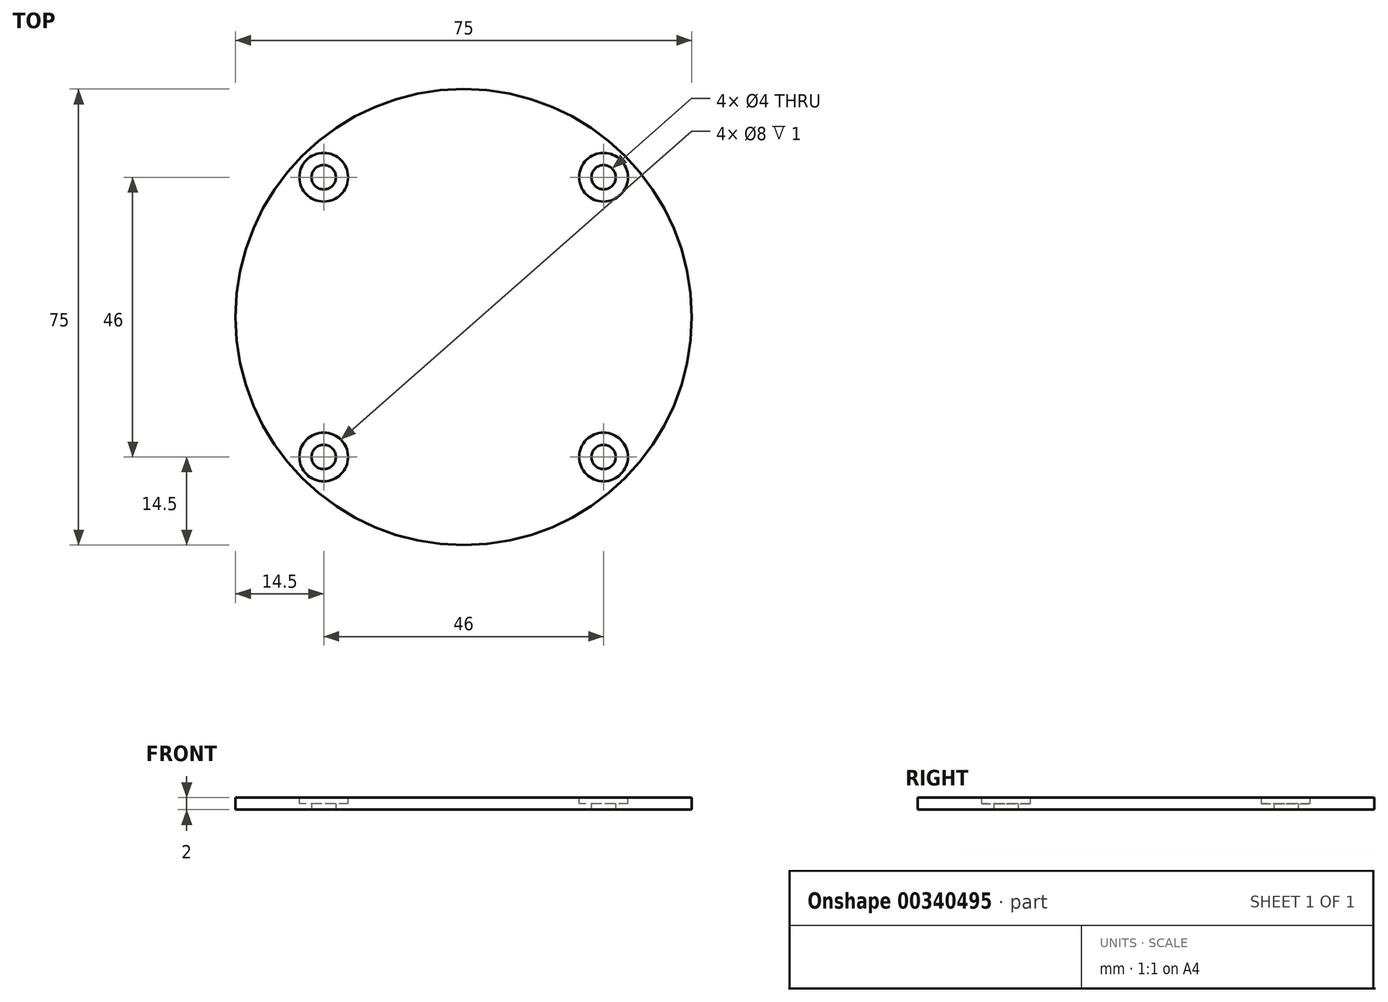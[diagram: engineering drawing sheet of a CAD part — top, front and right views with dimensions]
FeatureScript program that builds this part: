
annotation { "Feature Type Name" : "Feature", "Feature Type Description" : "" }
export const myFeature = defineFeature(function(context is Context, id is Id, definition is map)
    precondition{}
    {
        {
            var Q0;
            Q0=qCreatedBy(makeId("Top.planeOp"),FACE);
            var sketch = newSketch(context, id + "F0", { "sketchPlane" : qUnion([Q0])});
            skCircle(sketch, "E0", {"center": v(0, 0) * mm, "radius": 37.5 * mm});
            skCircle(sketch, "E1", {"center": v(-23, 23) * mm, "radius": 2 * mm});
            skCircle(sketch, "E2", {"center": v(-23, -23) * mm, "radius": 2 * mm});
            skCircle(sketch, "E3", {"center": v(23, -23) * mm, "radius": 2 * mm});
            skCircle(sketch, "E4", {"center": v(23, 23) * mm, "radius": 2 * mm});
            skSolve(sketch);
        }
        {
            var Q0;
            Q0=qSketchRegion(id+"F0",true);
            extrude(context, id + "F1", {"entities" : qUnion([Q0]), "depth" : 2 * mm});
        }
        {
            var Q0;
            Q0=makeQuery(id+"F1.opExtrude","CAP_FACE",FACE,{"disambiguationData":[OSD([sQuery(id+"F0.wireOp",EDGE,"E0"),sQuery(id+"F0.wireOp",EDGE,"E1"),sQuery(id+"F0.wireOp",EDGE,"E2"),sQuery(id+"F0.wireOp",EDGE,"E3"),sQuery(id+"F0.wireOp",EDGE,"E4")])],"isStart":false});
            var sketch = newSketch(context, id + "F2", { "sketchPlane" : qUnion([Q0])});
            skCircle(sketch, "E5", {"center": v(-23, 23) * mm, "radius": 4 * mm});
            skCircle(sketch, "E6", {"center": v(23, 23) * mm, "radius": 4 * mm});
            skCircle(sketch, "E7", {"center": v(-23, -23) * mm, "radius": 4 * mm});
            skCircle(sketch, "E8", {"center": v(23, -23) * mm, "radius": 4 * mm});
            skSolve(sketch);
        }
        {
            var Q0;
            Q0=qSketchRegion(id+"F2",true);
            extrude(context, id + "F3", {"entities" : qUnion([Q0]), "operationType" : NewBodyOperationType.REMOVE, "oppositeDirection" : true, "depth" : 1 * mm});
        }
    });
